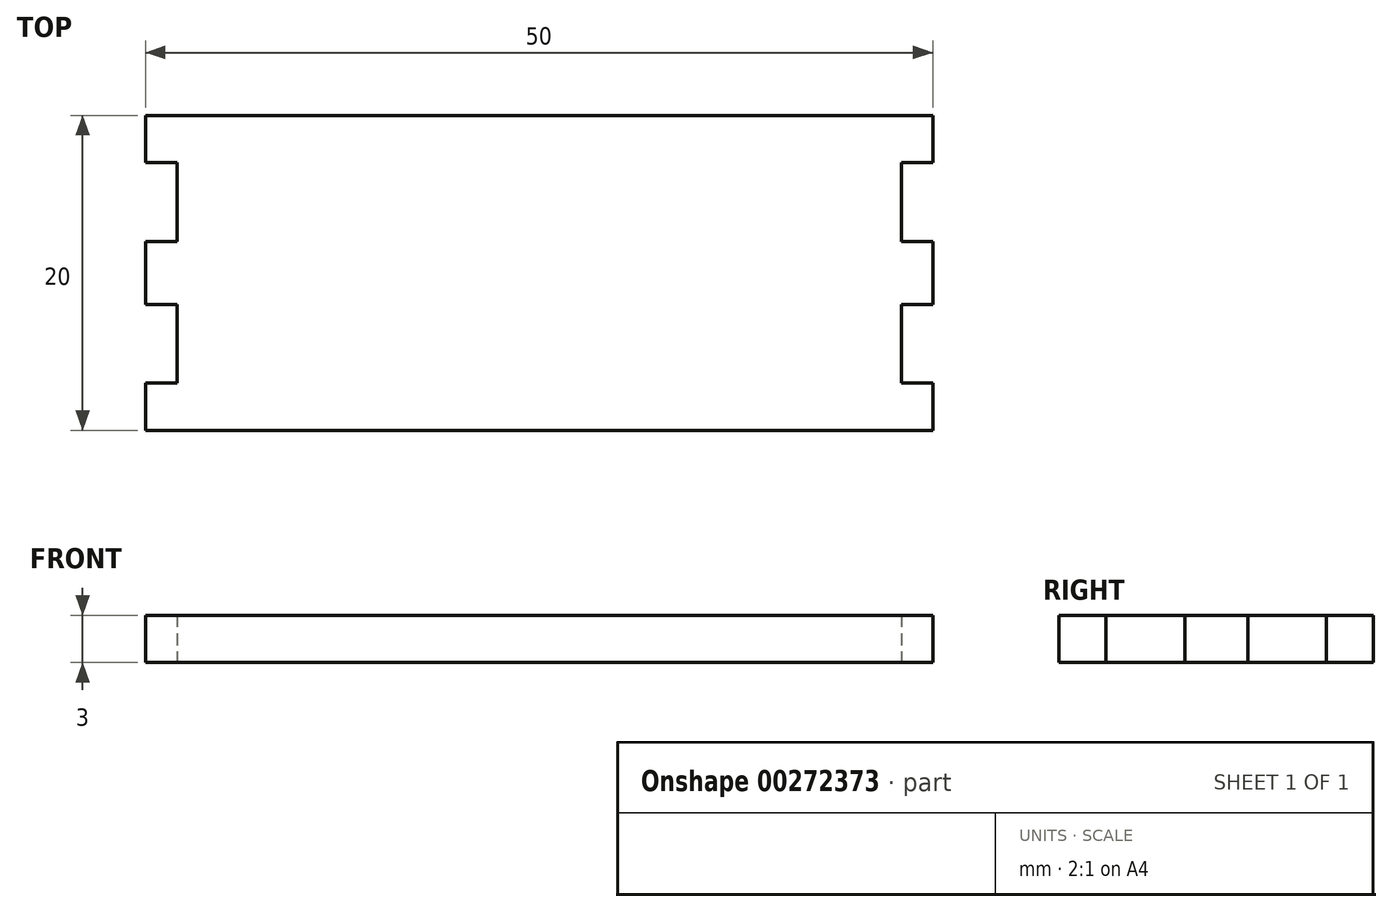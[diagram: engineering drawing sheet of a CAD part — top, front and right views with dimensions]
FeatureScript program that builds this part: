
annotation { "Feature Type Name" : "Feature", "Feature Type Description" : "" }
export const myFeature = defineFeature(function(context is Context, id is Id, definition is map)
    precondition{}
    {
        {
            var Q0;
            Q0=qCreatedBy(makeId("Top.planeOp"),FACE);
            var sketch = newSketch(context, id + "F0", { "sketchPlane" : qUnion([Q0])});
            skLineSegment(sketch, "E0.bottom", {"start": v(25, 10) * mm, "end": v(-25, 10) * mm});
            skLineSegment(sketch, "E0.top", {"start": v(25, -10) * mm, "end": v(-25, -10) * mm});
            skPoint(sketch, "E0.middle", {"position": v(0, 0) * mm});
            skLineSegment(sketch, "E1", {"start": v(0, 10) * mm, "end": v(0, -10) * mm, "construction": true});
            skLineSegment(sketch, "E2", {"start": v(-25, 0) * mm, "end": v(25, 0) * mm, "construction": true});
            skLineSegment(sketch, "E3", {"start": v(-25, 10) * mm, "end": v(-25, 7) * mm});
            skLineSegment(sketch, "E4", {"start": v(-25, 7) * mm, "end": v(-23, 7) * mm});
            skLineSegment(sketch, "E5", {"start": v(-23, 7) * mm, "end": v(-23, 2) * mm});
            skLineSegment(sketch, "E6", {"start": v(-23, 2) * mm, "end": v(-25, 2) * mm});
            skLineSegment(sketch, "E7", {"start": v(-25, 2) * mm, "end": v(-25, 0) * mm});
            skLineSegment(sketch, "E8.MirrorCS", {"start": v(-25, -2) * mm, "end": v(-25, 0) * mm});
            skLineSegment(sketch, "E9.MirrorCS", {"start": v(-23, -2) * mm, "end": v(-25, -2) * mm});
            skLineSegment(sketch, "E10.MirrorCS", {"start": v(-23, -7) * mm, "end": v(-23, -2) * mm});
            skLineSegment(sketch, "E11.MirrorCS", {"start": v(-25, -10) * mm, "end": v(-25, -7) * mm});
            skLineSegment(sketch, "E12.MirrorCS", {"start": v(-25, -7) * mm, "end": v(-23, -7) * mm});
            skLineSegment(sketch, "E13.MirrorCS", {"start": v(25, 2) * mm, "end": v(25, 0) * mm});
            skLineSegment(sketch, "E14.MirrorCS", {"start": v(23, 2) * mm, "end": v(25, 2) * mm});
            skLineSegment(sketch, "E15.MirrorCS", {"start": v(23, 7) * mm, "end": v(23, 2) * mm});
            skLineSegment(sketch, "E16.MirrorCS", {"start": v(25, 10) * mm, "end": v(25, 7) * mm});
            skLineSegment(sketch, "E17.MirrorCS", {"start": v(25, 7) * mm, "end": v(23, 7) * mm});
            skLineSegment(sketch, "E18.MirrorCS", {"start": v(25, -2) * mm, "end": v(25, 0) * mm});
            skLineSegment(sketch, "E19.MirrorCS", {"start": v(25, -10) * mm, "end": v(25, -7) * mm});
            skLineSegment(sketch, "E20.MirrorCS", {"start": v(25, -7) * mm, "end": v(23, -7) * mm});
            skLineSegment(sketch, "E21.MirrorCS", {"start": v(23, -7) * mm, "end": v(23, -2) * mm});
            skLineSegment(sketch, "E22.MirrorCS", {"start": v(23, -2) * mm, "end": v(25, -2) * mm});
            skSolve(sketch);
        }
        {
            var Q0;
            Q0=makeQuery(id+"F0.imprint","IMPRINT",FACE,{"disambiguationData":[TD([[makeQuery(id+"F0.imprint","IMPRINT",EDGE,{"derivedFrom":sQuery(id+"F0.wireOp",EDGE,"E0.bottom")}),1.0]])]});
            extrude(context, id + "F1", {"entities" : qUnion([Q0]), "depth" : 3 * mm});
        }
    });
